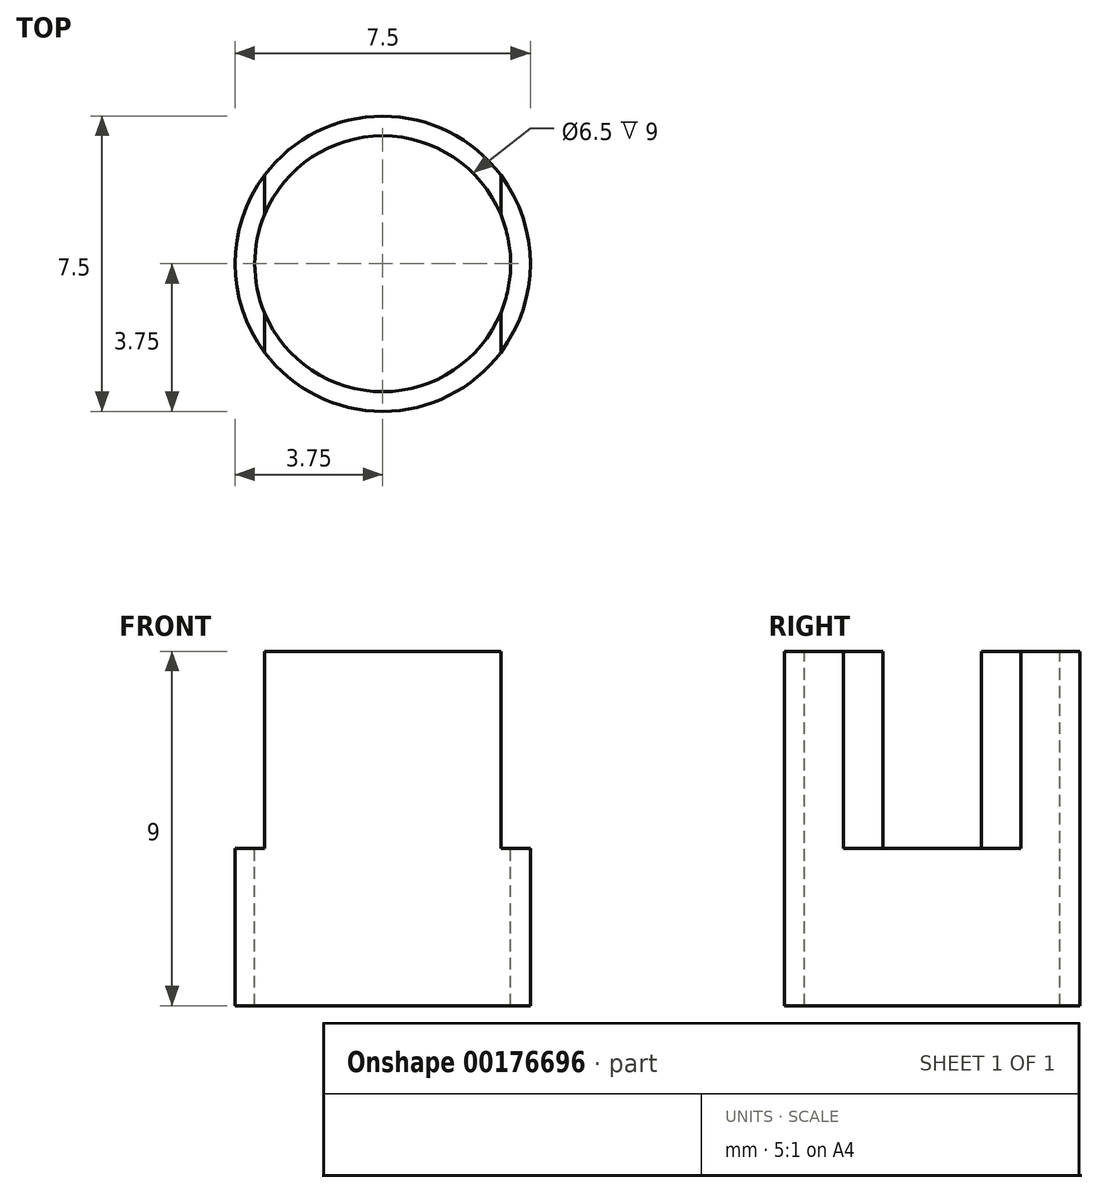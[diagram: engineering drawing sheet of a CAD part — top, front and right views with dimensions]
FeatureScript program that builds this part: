
annotation { "Feature Type Name" : "Feature", "Feature Type Description" : "" }
export const myFeature = defineFeature(function(context is Context, id is Id, definition is map)
    precondition{}
    {
        {
            var Q0;
            Q0=qCreatedBy(makeId("Top.planeOp"),FACE);
            var sketch = newSketch(context, id + "F0", { "sketchPlane" : qUnion([Q0])});
            skCircle(sketch, "E0", {"center": v(0, 0) * mm, "radius": 3.75 * mm});
            skSolve(sketch);
        }
        {
            var Q0;
            Q0=makeQuery(id+"F0.imprint","IMPRINT",FACE,{"disambiguationData":[TD([[makeQuery(id+"F0.imprint","IMPRINT",EDGE,{"derivedFrom":sQuery(id+"F0.wireOp",EDGE,"E0")}),1.0]])]});
            extrude(context, id + "F1", {"entities" : qUnion([Q0]), "depth" : 4 * mm});
        }
        {
            var Q0;
            Q0=makeQuery(id+"F1.opExtrude","CAP_FACE",FACE,{"disambiguationData":[OSD([sQuery(id+"F0.wireOp",EDGE,"E0")])],"isStart":false});
            var sketch = newSketch(context, id + "F2", { "sketchPlane" : qUnion([Q0])});
            skCircle(sketch, "E1", {"center": v(0, 0) * mm, "radius": 3.25 * mm});
            skLineSegment(sketch, "E2.bottom", {"start": v(3, -3.75) * mm, "end": v(-3, -3.75) * mm});
            skLineSegment(sketch, "E2.top", {"start": v(3, 3.75) * mm, "end": v(-3, 3.75) * mm});
            skLineSegment(sketch, "E2.left", {"start": v(3, -3.75) * mm, "end": v(3, -1.25) * mm});
            skLineSegment(sketch, "E2.right", {"start": v(-3, -3.75) * mm, "end": v(-3, -1.25) * mm});
            skLineSegment(sketch, "E3.trimOffspring", {"start": v(-3, 1.25) * mm, "end": v(-3, 3.75) * mm});
            skLineSegment(sketch, "E4.trimOffspring", {"start": v(3, 1.25) * mm, "end": v(3, 3.75) * mm});
            skSolve(sketch);
        }
        {
            var Q0;
            Q0=makeQuery(id+"F2.imprint","IMPRINT",FACE,{"disambiguationData":[TD([[makeQuery(id+"F2.imprint","IMPRINT",EDGE,{"derivedFrom":sQuery(id+"F2.wireOp",EDGE,"E1")}),1.0]])]});
            extrude(context, id + "F3", {"entities" : qUnion([Q0]), "operationType" : NewBodyOperationType.REMOVE, "endBound" : BoundingType.SYMMETRIC, "oppositeDirection" : true, "depth" : 10 * mm});
        }
        {
            var Q0;
            {var subQ4=sQuery(id+"F2.wireOp",EDGE,"E2.right");var subQ5=sQuery(id+"F2.wireOp",EDGE,"E1");var subQ6=makeQuery(id+"F2.imprint","INTERSECT",VERTEX,{"disambiguationData":[OD(1.0)],"derivedFrom":[subQ5,subQ4]});Q0=makeQuery(id+"F2.imprint","IMPRINT",FACE,{"disambiguationData":[TD([[makeQuery(id+"F2.imprint","IMPRINT",EDGE,{"disambiguationData":[TD([[subQ6,-1.0]])],"derivedFrom":subQ5}),-1.0]])]});}
            var Q1;
            {var subQ2=sQuery(id+"F2.wireOp",EDGE,"E3.trimOffspring");var subQ5=sQuery(id+"F2.wireOp",EDGE,"E1");var subQ8=makeQuery(id+"F2.imprint","INTERSECT",VERTEX,{"derivedFrom":[subQ5,subQ2]});Q1=makeQuery(id+"F2.imprint","IMPRINT",FACE,{"disambiguationData":[TD([[makeQuery(id+"F2.imprint","IMPRINT",EDGE,{"disambiguationData":[TD([[subQ8,1.0]])],"derivedFrom":subQ5}),-1.0]])]});}
            extrude(context, id + "F4", {"entities" : qUnion([Q0, Q1]), "operationType" : NewBodyOperationType.ADD, "depth" : 5 * mm});
        }
    });
